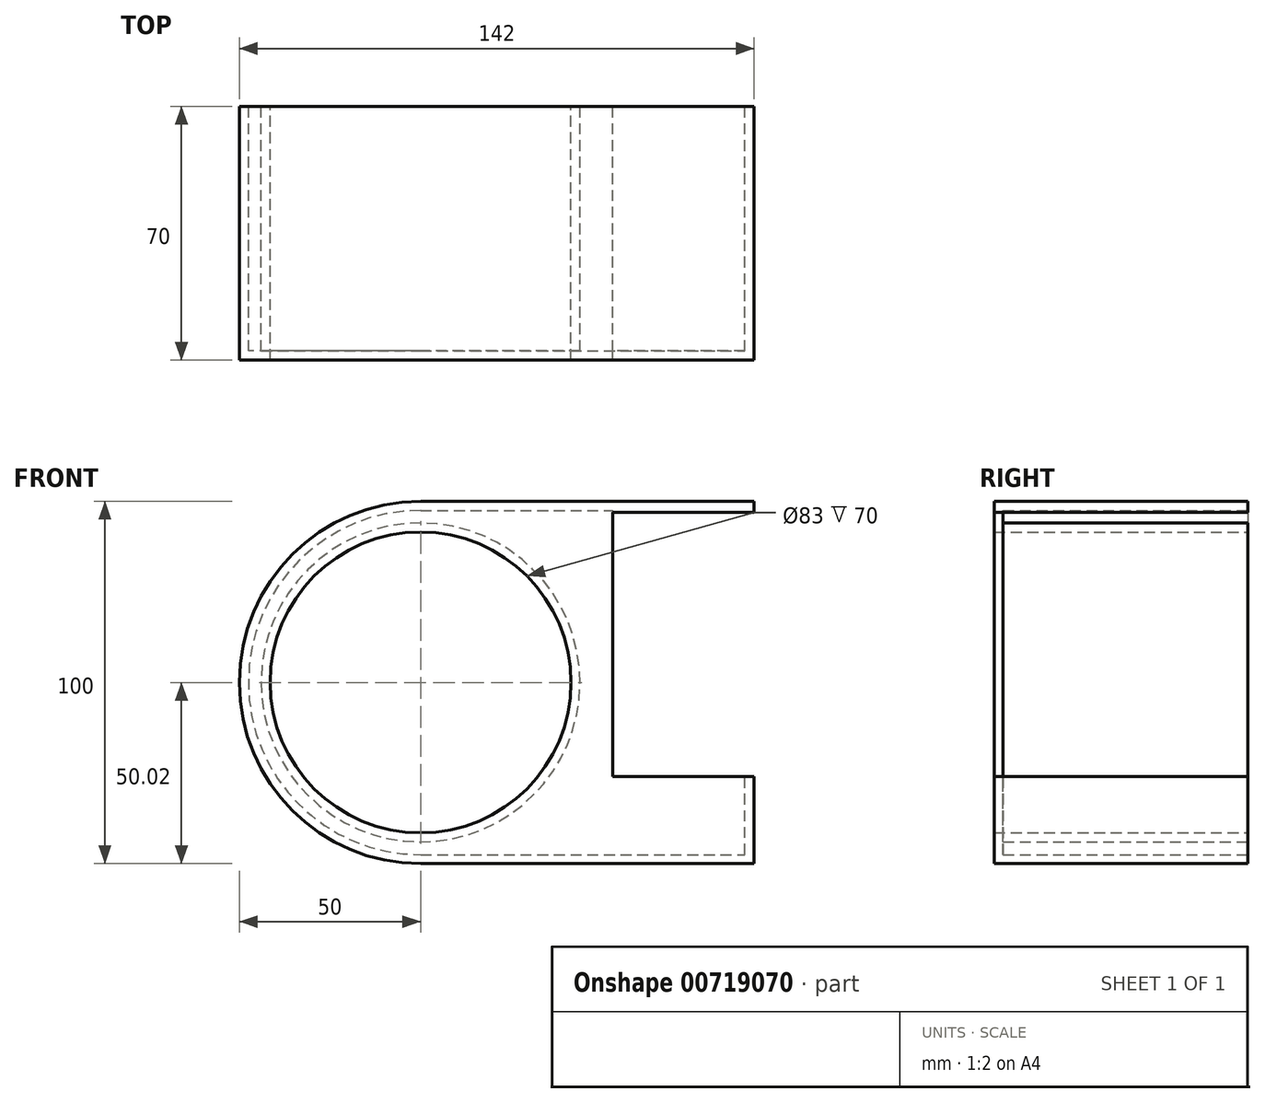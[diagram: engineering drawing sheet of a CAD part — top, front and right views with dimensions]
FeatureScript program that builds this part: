
annotation { "Feature Type Name" : "Feature", "Feature Type Description" : "" }
export const myFeature = defineFeature(function(context is Context, id is Id, definition is map)
    precondition{}
    {
        {
            var Q0;
            Q0=qCreatedBy(makeId("Front.planeOp"),FACE);
            var sketch = newSketch(context, id + "F0", { "sketchPlane" : qUnion([Q0])});
            skArc(sketch, "E0", {"start": v(-126.64, 57.97) * mm, "mid": v(-176.64, 7.97) * mm, "end": v(-126.64, -42.03) * mm});
            skLineSegment(sketch, "E1", {"start": v(-126.64, 57.97) * mm, "end": v(-34.64, 57.97) * mm});
            skLineSegment(sketch, "E2", {"start": v(-126.64, -42.03) * mm, "end": v(-34.64, -42.03) * mm});
            skLineSegment(sketch, "E3", {"start": v(-34.64, -42.03) * mm, "end": v(-34.64, -18.03) * mm});
            skPoint(sketch, "E4.end.orphan", {"position": v(-176.64, 7.97) * mm});
            skLineSegment(sketch, "E5", {"start": v(-34.64, -18.03) * mm, "end": v(-73.64, -18.03) * mm});
            skLineSegment(sketch, "E6", {"start": v(-73.64, -18.03) * mm, "end": v(-73.64, 54.97) * mm});
            skPoint(sketch, "E7.start.orphan", {"position": v(-34.64, 7.97) * mm});
            skLineSegment(sketch, "E8", {"start": v(-73.64, 54.97) * mm, "end": v(-34.64, 54.97) * mm});
            skLineSegment(sketch, "E9.trimOffspring", {"start": v(-34.64, 54.97) * mm, "end": v(-34.64, 57.97) * mm});
            skSolve(sketch);
        }
        {
            var Q0;
            Q0=qSketchRegion(id+"F0",true);
            extrude(context, id + "F1", {"entities" : qUnion([Q0]), "depth" : 70 * mm, "offsetDistance" : 25 * mm});
        }
        {
            var Q0;
            Q0=qCreatedBy(makeId("Front.planeOp"),FACE);
            var sketch = newSketch(context, id + "F2", { "sketchPlane" : qUnion([Q0])});
            skCircle(sketch, "E10", {"center": v(-126.64, 8) * mm, "radius": 41.5 * mm});
            skCircle(sketch, "E11.0", {"center": v(-126.64, 8) * mm, "radius": 43.1 * mm});
            skSolve(sketch);
        }
        {
            var Q0;
            Q0=sQuery(id+"F2.wireOp",VERTEX,"E10.center");
            var Q1;
            Q1=makeQuery(id+"F1.opExtrude","SWEPT_BODY",BODY,{"disambiguationData":[OSD([sQuery(id+"F0.wireOp",EDGE,"E0"),sQuery(id+"F0.wireOp",EDGE,"E1"),sQuery(id+"F0.wireOp",EDGE,"E2"),sQuery(id+"F0.wireOp",EDGE,"E3"),sQuery(id+"F0.wireOp",EDGE,"E5"),sQuery(id+"F0.wireOp",EDGE,"E6"),sQuery(id+"F0.wireOp",EDGE,"E8"),sQuery(id+"F0.wireOp",EDGE,"E9.trimOffspring")])]});
            hole(context, id + "F3", {"style" : HoleStyle.SIMPLE, "endStyle" : HoleEndStyle.THROUGH, "oppositeDirection" : true, "holeDiameter" : 83 * mm, "majorDiameter" : 5 * mm, "isTappedThrough" : true, "tappedDepth" : 12 * mm, "tapClearance" : 3, "startFromSketch" : true, "locations" : qUnion([Q0]), "scope" : qUnion([Q1])});
        }
        {
            var Q0;
            Q0=makeQuery(id+"F1.opExtrude","CAP_FACE",FACE,{"disambiguationData":[OSD([sQuery(id+"F0.wireOp",EDGE,"E0"),sQuery(id+"F0.wireOp",EDGE,"E1"),sQuery(id+"F0.wireOp",EDGE,"E2"),sQuery(id+"F0.wireOp",EDGE,"E3"),sQuery(id+"F0.wireOp",EDGE,"E5"),sQuery(id+"F0.wireOp",EDGE,"E6"),sQuery(id+"F0.wireOp",EDGE,"E8"),sQuery(id+"F0.wireOp",EDGE,"E9.trimOffspring")])],"isStart":true});
            var Q1;
            Q1=makeQuery(id+"F1.opExtrude","SWEPT_FACE",FACE,{"disambiguationData":[OSD([sQuery(id+"F0.wireOp",EDGE,"E6")])]});
            var Q2;
            Q2=makeQuery(id+"F3.hole-0.boolean.opBoolean","COPY",FACE,{"derivedFrom":makeQuery(id+"F3.hole-0.opRevolve","SWEPT_FACE",FACE,{"disambiguationData":[OSD([sQuery(id+"F3.hole-0.sketch.wireOp",EDGE,"core_line_2")])]})});
            var Q3;
            Q3=makeQuery(id+"F1.opExtrude","SWEPT_FACE",FACE,{"disambiguationData":[OSD([sQuery(id+"F0.wireOp",EDGE,"E5")])]});
            var Q4;
            Q4=makeQuery(id+"F1.opExtrude","SWEPT_FACE",FACE,{"disambiguationData":[OSD([sQuery(id+"F0.wireOp",EDGE,"E3")])]});
            shell(context, id + "F4", {"entities" : qUnion([Q0, Q1, Q2, Q3, Q4]), "thickness" : 2.5 * mm});
        }
    });
